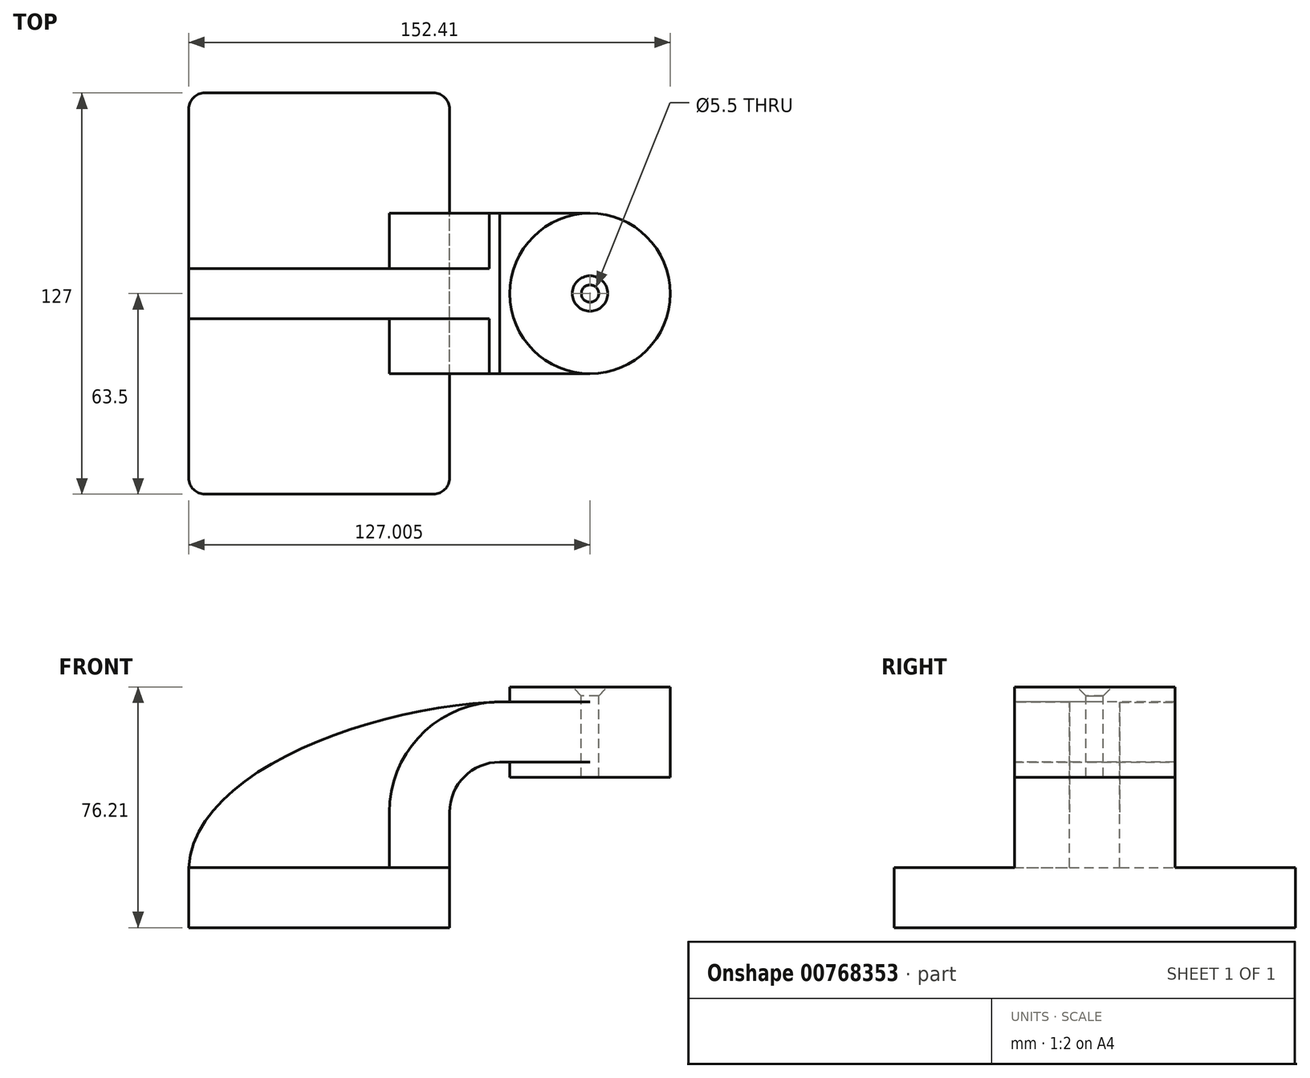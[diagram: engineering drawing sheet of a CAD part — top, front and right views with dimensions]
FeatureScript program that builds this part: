
annotation { "Feature Type Name" : "Feature", "Feature Type Description" : "" }
export const myFeature = defineFeature(function(context is Context, id is Id, definition is map)
    precondition{}
    {
        {
            var Q0;
            Q0=qCreatedBy(makeId("Front.planeOp"),FACE);
            var sketch = newSketch(context, id + "F0", { "sketchPlane" : qUnion([Q0])});
            skLineSegment(sketch, "E0.rect.bottom", {"start": v(-41.28, 9.52) * mm, "end": v(41.28, 9.52) * mm});
            skLineSegment(sketch, "E0.rect.top", {"start": v(-41.28, -9.52) * mm, "end": v(41.28, -9.52) * mm});
            skLineSegment(sketch, "E0.rect.left", {"start": v(-41.28, 9.52) * mm, "end": v(-41.28, -9.52) * mm});
            skLineSegment(sketch, "E0.rect.right", {"start": v(41.28, 9.52) * mm, "end": v(41.28, -9.52) * mm});
            skPoint(sketch, "E0.rect.middle", {"position": v(0, 0) * mm});
            skLineSegment(sketch, "E1", {"start": v(41.28, 9.52) * mm, "end": v(41.28, 27) * mm});
            skArc(sketch, "E2", {"start": v(41.28, 27) * mm, "mid": v(45.92, 38.23) * mm, "end": v(57.15, 42.88) * mm});
            skLineSegment(sketch, "E3", {"start": v(57.15, 42.88) * mm, "end": v(85.72, 42.88) * mm});
            skLineSegment(sketch, "E4.rect.bottom", {"start": v(60.32, 38.1) * mm, "end": v(111.12, 38.1) * mm});
            skLineSegment(sketch, "E4.rect.top", {"start": v(60.32, 66.68) * mm, "end": v(111.12, 66.68) * mm});
            skLineSegment(sketch, "E4.rect.left", {"start": v(60.32, 38.1) * mm, "end": v(60.32, 66.68) * mm});
            skLineSegment(sketch, "E4.rect.right", {"start": v(111.13, 38.1) * mm, "end": v(111.12, 66.68) * mm});
            skPoint(sketch, "E4.rect.middle", {"position": v(85.72, 52.39) * mm});
            skLineSegment(sketch, "E5.0", {"start": v(57.15, 61.93) * mm, "end": v(85.72, 61.93) * mm});
            skArc(sketch, "E5.1", {"start": v(22.23, 27) * mm, "mid": v(32.45, 51.7) * mm, "end": v(57.15, 61.93) * mm});
            skLineSegment(sketch, "E5.2", {"start": v(22.23, 9.52) * mm, "end": v(22.23, 27) * mm});
            skLineSegment(sketch, "E6", {"start": v(85.72, 38.1) * mm, "end": v(85.72, 66.68) * mm});
            skFitSpline(sketch, "E7", {"points": [v(-41.28, 9.53) * mm, v(57.15, 61.93) * mm], "startDerivative": vector(5.2, 92.34) * mm, "endDerivative": vector(120.92, 4.22) * mm});
            skSolve(sketch);
        }
        {
            var Q0;
            Q0=makeQuery(id+"F0.imprint","IMPRINT",FACE,{"disambiguationData":[TD([[makeQuery(id+"F0.imprint","IMPRINT",EDGE,{"derivedFrom":sQuery(id+"F0.wireOp",EDGE,"E0.rect.top")}),1.0]])]});
            extrude(context, id + "F1", {"entities" : qUnion([Q0]), "endBound" : BoundingType.SYMMETRIC, "depth" : 127 * mm});
        }
        {
            var Q0;
            {var subQ9=sQuery(id+"F0.wireOp",EDGE,"E1");Q0=makeQuery(id+"F0.imprint","IMPRINT",FACE,{"disambiguationData":[TD([[makeQuery(id+"F0.imprint","IMPRINT",EDGE,{"derivedFrom":subQ9}),1.0]])]});}
            var Q1;
            {var subQ0=sQuery(id+"F0.wireOp",EDGE,"E6");var subQ1=sQuery(id+"F0.wireOp",EDGE,"E3");var subQ2=makeQuery(id+"F0.imprint","INTERSECT",VERTEX,{"derivedFrom":[subQ1,subQ0]});Q1=makeQuery(id+"F0.imprint","IMPRINT",FACE,{"disambiguationData":[TD([[makeQuery(id+"F0.imprint","IMPRINT",EDGE,{"disambiguationData":[TD([[subQ2,1.0]])],"derivedFrom":subQ1}),1.0]])]});}
            extrude(context, id + "F2", {"entities" : qUnion([Q0, Q1]), "operationType" : NewBodyOperationType.ADD, "endBound" : BoundingType.SYMMETRIC, "depth" : 50.8 * mm});
        }
        {
            var Q0;
            {var subQ3=sQuery(id+"F0.wireOp",EDGE,"E5.2");Q0=makeQuery(id+"F0.imprint","IMPRINT",FACE,{"disambiguationData":[TD([[makeQuery(id+"F0.imprint","IMPRINT",EDGE,{"derivedFrom":subQ3}),1.0]])]});}
            extrude(context, id + "F3", {"entities" : qUnion([Q0]), "operationType" : NewBodyOperationType.ADD, "endBound" : BoundingType.SYMMETRIC, "depth" : 15.88 * mm});
        }
        {
            var Q0;
            {var subQ5=sQuery(id+"F0.wireOp",EDGE,"E4.rect.right");Q0=makeQuery(id+"F0.imprint","IMPRINT",FACE,{"disambiguationData":[TD([[makeQuery(id+"F0.imprint","IMPRINT",EDGE,{"derivedFrom":subQ5}),1.0]])]});}
            var Q1;
            Q1=sQuery(id+"F0.wireOp",EDGE,"E6");
            revolve(context, id + "F4", {"operationType" : NewBodyOperationType.ADD, "entities" : qUnion([Q0]), "axis" : qUnion([Q1]), "revolveType" : RevolveType.FULL});
        }
        {
            var Q0;
            Q0=makeQuery(id+"F1.opExtrude","CAP_EDGE",EDGE,{"disambiguationData":[OSD([sQuery(id+"F0.wireOp",EDGE,"E0.rect.right")])],"isStart":false});
            var Q1;
            Q1=makeQuery(id+"F1.opExtrude","CAP_EDGE",EDGE,{"disambiguationData":[OSD([sQuery(id+"F0.wireOp",EDGE,"E0.rect.left")])],"isStart":false});
            var Q2;
            Q2=makeQuery(id+"F1.opExtrude","CAP_EDGE",EDGE,{"disambiguationData":[OSD([sQuery(id+"F0.wireOp",EDGE,"E0.rect.right")])],"isStart":true});
            var Q3;
            Q3=makeQuery(id+"F1.opExtrude","CAP_EDGE",EDGE,{"disambiguationData":[OSD([sQuery(id+"F0.wireOp",EDGE,"E0.rect.left")])],"isStart":true});
            fillet(context, id + "F5", {"entities" : qUnion([Q0, Q1, Q2, Q3]), "radius" : 5.08 * mm, "tangentPropagation" : true, "allowEdgeOverflow" : false});
        }
        {
            var Q0;
            Q0=makeQuery(id+"F4.opRevolve","SWEPT_FACE",FACE,{"disambiguationData":[OSD([sQuery(id+"F0.wireOp",EDGE,"E4.rect.top")])]});
            var sketch = newSketch(context, id + "F6", { "sketchPlane" : qUnion([Q0])});
            skPoint(sketch, "E8", {"position": v(85.72, 0) * mm});
            skSolve(sketch);
        }
        {
            var Q0;
            Q0=sQuery(id+"F6.wireOp",VERTEX,"E8");
            var Q1;
            Q1=makeQuery(id+"F1.opExtrude","SWEPT_BODY",BODY,{"disambiguationData":[OSD([sQuery(id+"F0.wireOp",EDGE,"E0.rect.bottom"),sQuery(id+"F0.wireOp",EDGE,"E0.rect.top"),sQuery(id+"F0.wireOp",EDGE,"E0.rect.left"),sQuery(id+"F0.wireOp",EDGE,"E0.rect.right")])]});
            hole(context, id + "F7", {"style" : HoleStyle.C_SINK, "endStyle" : HoleEndStyle.THROUGH, "standardTappedOrClearance" : lookupTablePath({ "standard" : "ISO", "fit" : "Normal", "size" : "M5", "type" : "Clearance" }), "standardBlindInLast" : lookupTablePath({ "fit" : "Standard", "standard" : "ISO", "size" : "M5", "type" : "Clearance" }), "holeDiameter" : 5.5 * mm, "cSinkDiameter" : 11.2 * mm, "cSinkAngle" : 90 * degree, "majorDiameter" : 6.35 * mm, "isTappedThrough" : true, "tappedDepth" : 12.7 * mm, "tapClearance" : 3, "locations" : qUnion([Q0]), "scope" : qUnion([Q1])});
        }
    });
